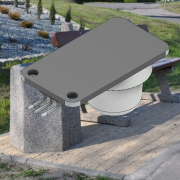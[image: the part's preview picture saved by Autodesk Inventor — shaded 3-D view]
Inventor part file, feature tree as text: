
AUTODESK INVENTOR PART (.ipt)
format: ipt  version: 2021 (Build 250183000, 183)  size: 306,176 bytes
history: mixed  units: mm
features: projected_geometry x2, extrude x1, sketch x1, sweep x1, imported_body x1
ambient origin geometry x8: Origin, YZ Plane, XZ Plane, XY Plane, X Axis, Y Axis, Z Axis, Center Point
bodies: Solid1 (imported_parasolid)
feature tree (6):
  extrude  "Extrusion1"  [1 undecoded]
  sketch  "Sketch1"  dims[d0=2.0mm d1=0.0mm]
  projected_geometry  "Projected Loop1"
  projected_geometry  "Projected Loop2"
  sweep  "Sweep2"
  imported_body  NMx_Import_Brep_tag  [imported B-rep: ~100 faces, bbox_mm=[21.3, 18.0, 42.167245]]
note: 1 required parameter value undecoded (feature->parameter linkage not recoverable at this tier; creation-order binding heuristic only, values carry confidence <= 0.55)
